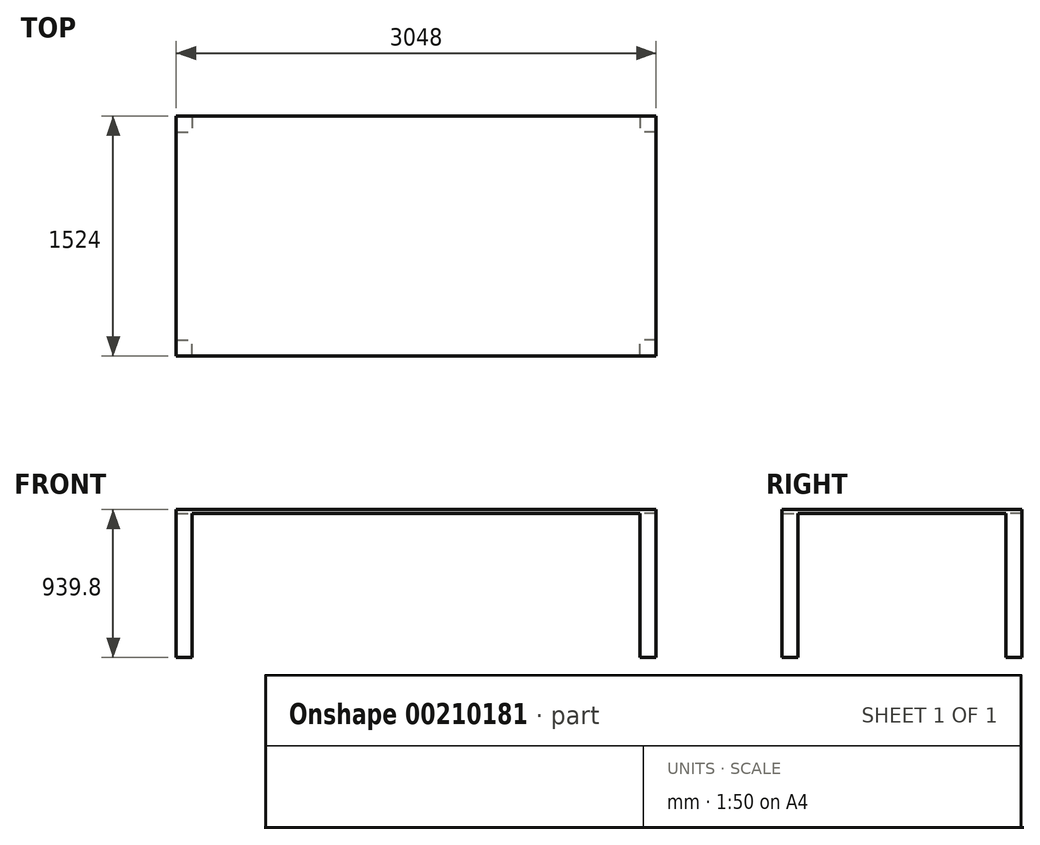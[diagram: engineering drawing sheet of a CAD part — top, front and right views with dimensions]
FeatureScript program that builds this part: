
annotation { "Feature Type Name" : "Feature", "Feature Type Description" : "" }
export const myFeature = defineFeature(function(context is Context, id is Id, definition is map)
    precondition{}
    {
        {
            var Q0;
            Q0=qCreatedBy(makeId("Top.planeOp"),FACE);
            var sketch = newSketch(context, id + "F0", { "sketchPlane" : qUnion([Q0])});
            skLineSegment(sketch, "E0.bottom", {"start": v(-1524, 762) * mm, "end": v(1524, 762) * mm});
            skLineSegment(sketch, "E0.top", {"start": v(-1524, -762) * mm, "end": v(1524, -762) * mm});
            skLineSegment(sketch, "E0.left", {"start": v(-1524, 762) * mm, "end": v(-1524, -762) * mm});
            skLineSegment(sketch, "E0.right", {"start": v(1524, 762) * mm, "end": v(1524, -762) * mm});
            skSolve(sketch);
        }
        {
            var Q0;
            Q0=makeQuery(id+"F0.imprint","IMPRINT",FACE,{"disambiguationData":[TD([[makeQuery(id+"F0.imprint","IMPRINT",EDGE,{"derivedFrom":sQuery(id+"F0.wireOp",EDGE,"E0.bottom")}),-1.0]])]});
            extrude(context, id + "F1", {"entities" : qUnion([Q0]), "depth" : 25.4 * mm});
        }
        {
            var Q0;
            Q0=qCreatedBy(makeId("Top.planeOp"),FACE);
            var sketch = newSketch(context, id + "F2", { "sketchPlane" : qUnion([Q0])});
            skLineSegment(sketch, "E1.bottom", {"start": v(-1524, 762) * mm, "end": v(-1422.4, 762) * mm});
            skLineSegment(sketch, "E1.top", {"start": v(-1524, 660.4) * mm, "end": v(-1422.4, 660.4) * mm});
            skLineSegment(sketch, "E1.left", {"start": v(-1524, 762) * mm, "end": v(-1524, 660.4) * mm});
            skLineSegment(sketch, "E1.right", {"start": v(-1422.4, 762) * mm, "end": v(-1422.4, 660.4) * mm});
            skLineSegment(sketch, "E2", {"start": v(0, 0) * mm, "end": v(-1722.14, 0) * mm, "construction": true});
            skLineSegment(sketch, "E3.MirrorCS", {"start": v(-1524, -660.4) * mm, "end": v(-1422.4, -660.4) * mm});
            skLineSegment(sketch, "E4.MirrorCS", {"start": v(-1524, -762) * mm, "end": v(-1422.4, -762) * mm});
            skLineSegment(sketch, "E5.MirrorCS", {"start": v(-1524, -762) * mm, "end": v(-1524, -660.4) * mm});
            skLineSegment(sketch, "E6.MirrorCS", {"start": v(-1422.4, -762) * mm, "end": v(-1422.4, -660.4) * mm});
            skLineSegment(sketch, "E7", {"start": v(0, 0) * mm, "end": v(0, 563.85) * mm, "construction": true});
            skLineSegment(sketch, "E8.MirrorCS", {"start": v(1524, 762) * mm, "end": v(1524, 660.4) * mm});
            skLineSegment(sketch, "E9.MirrorCS", {"start": v(1524, -660.4) * mm, "end": v(1422.4, -660.4) * mm});
            skLineSegment(sketch, "E10.MirrorCS", {"start": v(1524, 762) * mm, "end": v(1422.4, 762) * mm});
            skLineSegment(sketch, "E11.MirrorCS", {"start": v(1524, 660.4) * mm, "end": v(1422.4, 660.4) * mm});
            skLineSegment(sketch, "E12.MirrorCS", {"start": v(1524, -762) * mm, "end": v(1524, -660.4) * mm});
            skLineSegment(sketch, "E13.MirrorCS", {"start": v(1524, -762) * mm, "end": v(1422.4, -762) * mm});
            skLineSegment(sketch, "E14.MirrorCS", {"start": v(1422.4, 762) * mm, "end": v(1422.4, 660.4) * mm});
            skLineSegment(sketch, "E15.MirrorCS", {"start": v(1422.4, -762) * mm, "end": v(1422.4, -660.4) * mm});
            skSolve(sketch);
        }
        {
            var Q0;
            Q0 = qSketchRegion(id + "F2", true);
            extrude(context, id + "F3", {"entities" : qUnion([Q0]), "operationType" : NewBodyOperationType.ADD, "oppositeDirection" : true, "depth" : 914.4 * mm});
        }
    });
